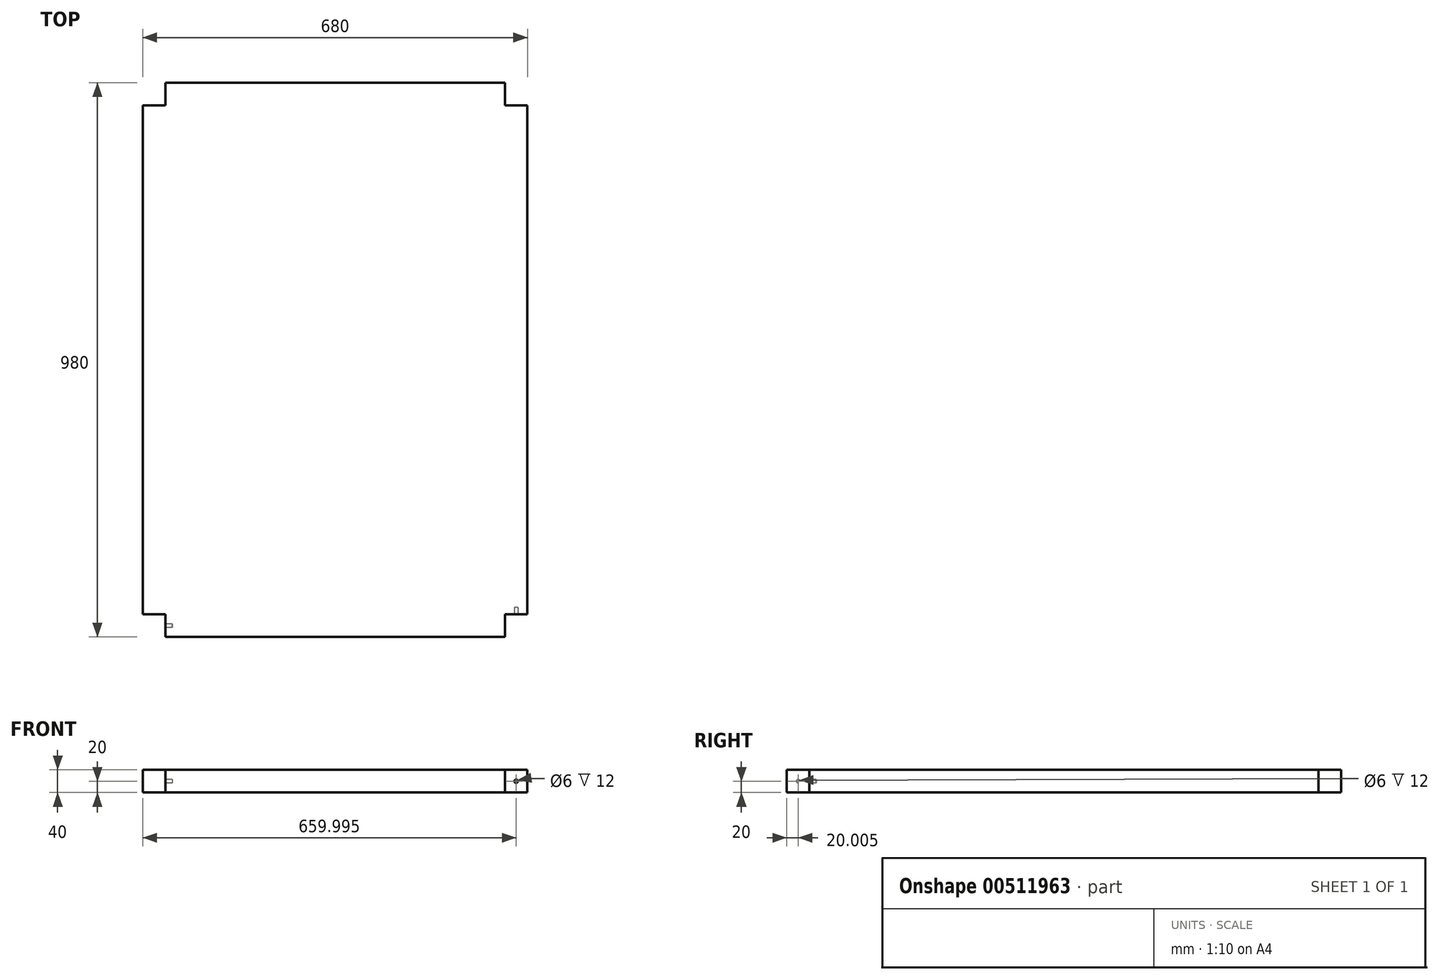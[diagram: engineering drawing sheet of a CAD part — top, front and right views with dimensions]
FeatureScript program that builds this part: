
annotation { "Feature Type Name" : "Feature", "Feature Type Description" : "" }
export const myFeature = defineFeature(function(context is Context, id is Id, definition is map)
    precondition{}
    {
        {
            var Q0;
            Q0=qCreatedBy(makeId("Top.planeOp"),FACE);
            var sketch = newSketch(context, id + "F0", { "sketchPlane" : qUnion([Q0])});
            skLineSegment(sketch, "E0.bottom", {"start": v(-662.47, 921.5) * mm, "end": v(17.53, 921.5) * mm});
            skLineSegment(sketch, "E0.top", {"start": v(-662.47, -58.5) * mm, "end": v(17.53, -58.5) * mm});
            skLineSegment(sketch, "E0.left", {"start": v(-662.47, 921.5) * mm, "end": v(-662.47, -58.5) * mm});
            skLineSegment(sketch, "E0.right", {"start": v(17.53, 921.5) * mm, "end": v(17.53, -58.5) * mm});
            skSolve(sketch);
        }
        {
            var Q0;
            Q0=makeQuery(id+"F0.imprint","IMPRINT",FACE,{"disambiguationData":[TD([[makeQuery(id+"F0.imprint","IMPRINT",EDGE,{"derivedFrom":sQuery(id+"F0.wireOp",EDGE,"E0.bottom")}),-1.0]])]});
            extrude(context, id + "F1", {"entities" : qUnion([Q0]), "depth" : 40 * mm, "offsetDistance" : 25 * mm});
        }
        {
            var Q0;
            Q0=makeQuery(id+"F1.opExtrude","CAP_FACE",FACE,{"disambiguationData":[OSD([sQuery(id+"F0.wireOp",EDGE,"E0.bottom"),sQuery(id+"F0.wireOp",EDGE,"E0.top"),sQuery(id+"F0.wireOp",EDGE,"E0.left"),sQuery(id+"F0.wireOp",EDGE,"E0.right")])],"isStart":false});
            var sketch = newSketch(context, id + "F2", { "sketchPlane" : qUnion([Q0])});
            skLineSegment(sketch, "E1.bottom", {"start": v(-662.47, 921.5) * mm, "end": v(-622.47, 921.5) * mm});
            skLineSegment(sketch, "E1.top", {"start": v(-662.47, 881.5) * mm, "end": v(-622.47, 881.5) * mm});
            skLineSegment(sketch, "E1.left", {"start": v(-662.47, 921.5) * mm, "end": v(-662.47, 881.5) * mm});
            skLineSegment(sketch, "E1.right", {"start": v(-622.47, 921.5) * mm, "end": v(-622.47, 881.5) * mm});
            skLineSegment(sketch, "E2.bottom", {"start": v(17.53, 921.5) * mm, "end": v(-22.47, 921.5) * mm});
            skLineSegment(sketch, "E2.top", {"start": v(17.53, 881.5) * mm, "end": v(-22.47, 881.5) * mm});
            skLineSegment(sketch, "E2.left", {"start": v(17.53, 921.5) * mm, "end": v(17.53, 881.5) * mm});
            skLineSegment(sketch, "E2.right", {"start": v(-22.47, 921.5) * mm, "end": v(-22.47, 881.5) * mm});
            skLineSegment(sketch, "E3.bottom", {"start": v(-662.47, -58.5) * mm, "end": v(-622.47, -58.5) * mm});
            skLineSegment(sketch, "E3.top", {"start": v(-662.47, -18.5) * mm, "end": v(-622.47, -18.5) * mm});
            skLineSegment(sketch, "E3.left", {"start": v(-662.47, -58.5) * mm, "end": v(-662.47, -18.5) * mm});
            skLineSegment(sketch, "E3.right", {"start": v(-622.47, -58.5) * mm, "end": v(-622.47, -18.5) * mm});
            skLineSegment(sketch, "E4.bottom", {"start": v(17.53, -58.5) * mm, "end": v(-22.47, -58.5) * mm});
            skLineSegment(sketch, "E4.top", {"start": v(17.53, -18.5) * mm, "end": v(-22.47, -18.5) * mm});
            skLineSegment(sketch, "E4.left", {"start": v(17.53, -58.5) * mm, "end": v(17.53, -18.5) * mm});
            skLineSegment(sketch, "E4.right", {"start": v(-22.47, -58.5) * mm, "end": v(-22.47, -18.5) * mm});
            skSolve(sketch);
        }
        {
            var Q0;
            Q0 = qSketchRegion(id + "F2", true);
            extrude(context, id + "F3", {"entities" : qUnion([Q0]), "operationType" : NewBodyOperationType.REMOVE, "oppositeDirection" : true, "depth" : 40 * mm, "offsetDistance" : 25 * mm});
        }
        {
            var Q0;
            Q0=makeQuery(id+"F3.boolean.opBoolean","COPY",FACE,{"derivedFrom":makeQuery(id+"F3.opExtrude","SWEPT_FACE",FACE,{"disambiguationData":[OSD([sQuery(id+"F2.wireOp",EDGE,"E4.top")])]})});
            var sketch = newSketch(context, id + "F4", { "sketchPlane" : qUnion([Q0])});
            skPoint(sketch, "E5.centerSnap0", {"position": v(-22.47, 20) * mm});
            skCircle(sketch, "E6", {"center": v(-2.47, 20) * mm, "radius": 3 * mm});
            skSolve(sketch);
        }
        {
            var Q0;
            Q0=makeQuery(id+"F4.imprint","IMPRINT",FACE,{"disambiguationData":[TD([[makeQuery(id+"F4.imprint","IMPRINT",EDGE,{"derivedFrom":sQuery(id+"F4.wireOp",EDGE,"E6")}),1.0]])]});
            var Q1;
            Q1=sQuery(id+"F4.wireOp",EDGE,"E6");
            extrude(context, id + "F5", {"entities" : qUnion([Q0]), "operationType" : NewBodyOperationType.REMOVE, "surfaceEntities" : qUnion([Q1]), "oppositeDirection" : true, "depth" : 12 * mm, "offsetDistance" : 25 * mm});
        }
        {
            var Q0;
            Q0=makeQuery(id+"F3.boolean.opBoolean","COPY",FACE,{"derivedFrom":makeQuery(id+"F3.opExtrude","SWEPT_FACE",FACE,{"disambiguationData":[OSD([sQuery(id+"F2.wireOp",EDGE,"E3.right")])]})});
            var sketch = newSketch(context, id + "F6", { "sketchPlane" : qUnion([Q0])});
            skCircle(sketch, "E7", {"center": v(38.5, 20) * mm, "radius": 3 * mm});
            skPoint(sketch, "E7.centerSnap0", {"position": v(38.5, 0) * mm});
            skSolve(sketch);
        }
        {
            var Q0;
            Q0=makeQuery(id+"F6.imprint","IMPRINT",FACE,{"disambiguationData":[TD([[makeQuery(id+"F6.imprint","IMPRINT",EDGE,{"derivedFrom":sQuery(id+"F6.wireOp",EDGE,"E7")}),1.0]])]});
            extrude(context, id + "F7", {"entities" : qUnion([Q0]), "operationType" : NewBodyOperationType.REMOVE, "oppositeDirection" : true, "depth" : 12 * mm, "offsetDistance" : 25 * mm});
        }
    });
